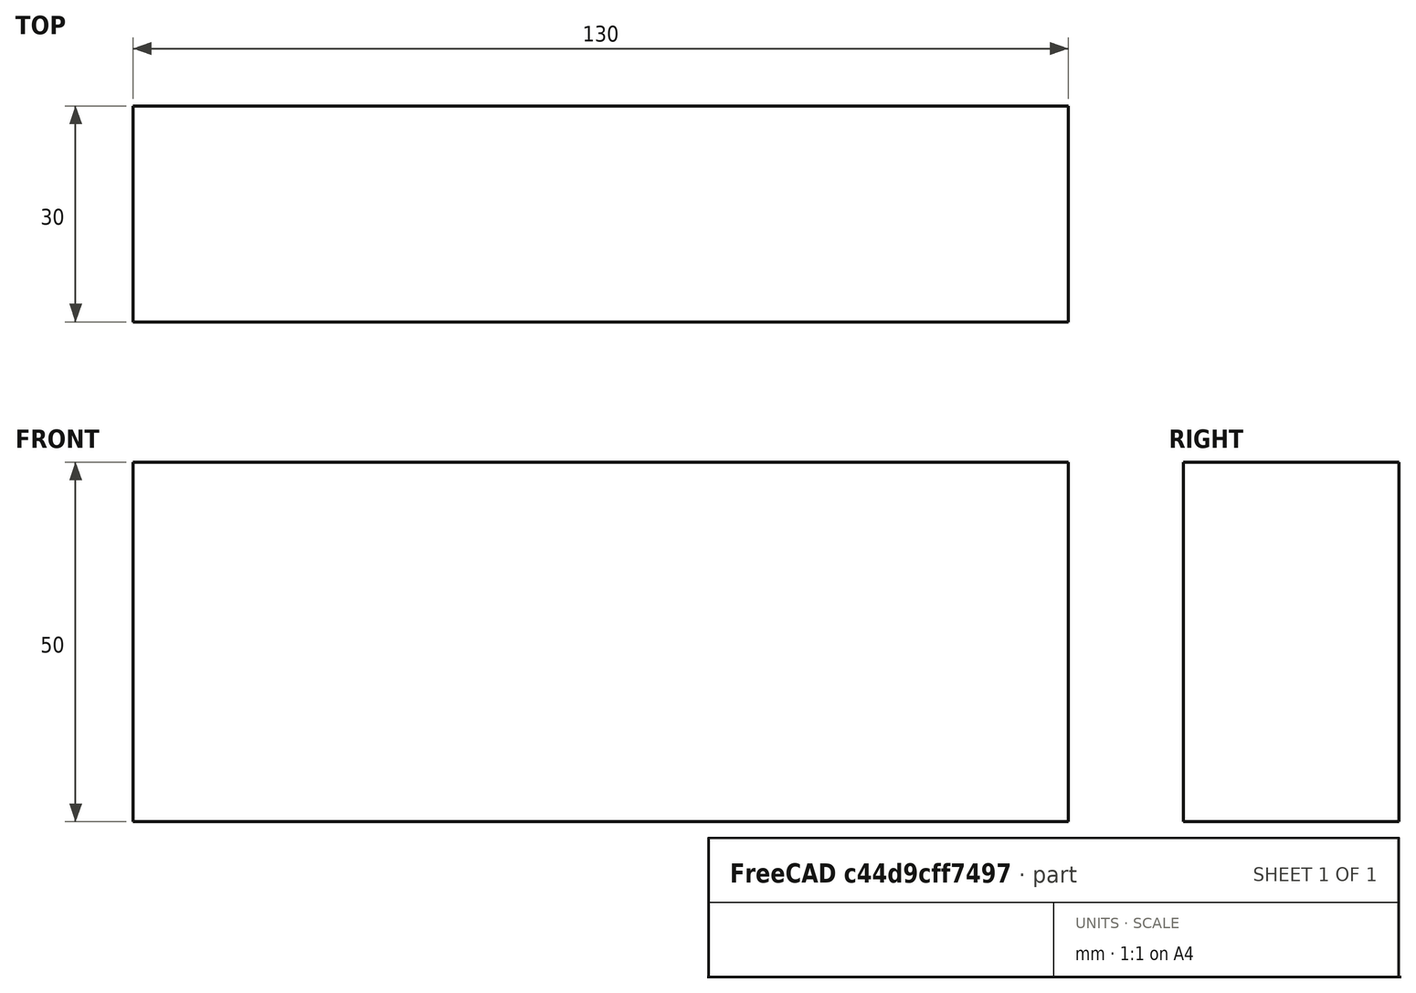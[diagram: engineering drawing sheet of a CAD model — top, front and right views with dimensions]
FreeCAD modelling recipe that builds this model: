
FCSTD DOCUMENT  (FreeCAD 0.15R4671 (Git))
Label: Flat Bar 130x30 EN10058 S235JR
License: All rights reserved
LicenseURL: http://en.wikipedia.org/wiki/All_rights_reserved
objects: Sketcher::SketchObject×1, Part::Extrusion×1
note: 2 computed .brp shape members not serialized (recipe doc carries the construction recipe); baked Part::Feature solids carry a one-line shape summary decoded from their .brp

FEATURE [Sketcher::SketchObject] Sketch
  sketch-geometry (4):
    g0: LineSegment StartX=-65 StartY=-15 StartZ=0 EndX=65 EndY=-15 EndZ=0
    g1: LineSegment StartX=65 StartY=-15 StartZ=0 EndX=65 EndY=15 EndZ=0
    g2: LineSegment StartX=65 StartY=15 StartZ=0 EndX=-65 EndY=15 EndZ=0
    g3: LineSegment StartX=-65 StartY=15 StartZ=0 EndX=-65 EndY=-15 EndZ=0
  constraints (12):
    c: Coincident(g0,g1)
    c: Coincident(g1,g2)
    c: Coincident(g2,g3)
    c: Coincident(g3,g0)
    c: Horizontal(g0)
    c: Horizontal(g2)
    c: Vertical(g1)
    c: Vertical(g3)
    c: Symmetric(g1,g2,g-2)
    c: Symmetric(g0,g1,g-1)
    c: DistanceY(g1) = 30
    c: DistanceX(g0) = 130
FEATURE [Part::Extrusion] Extrude  label="Flat Bar 130x30 EN10058 S235JR"
  Base = -> Sketch
  Dir = (0,0,50)
  Solid = true
